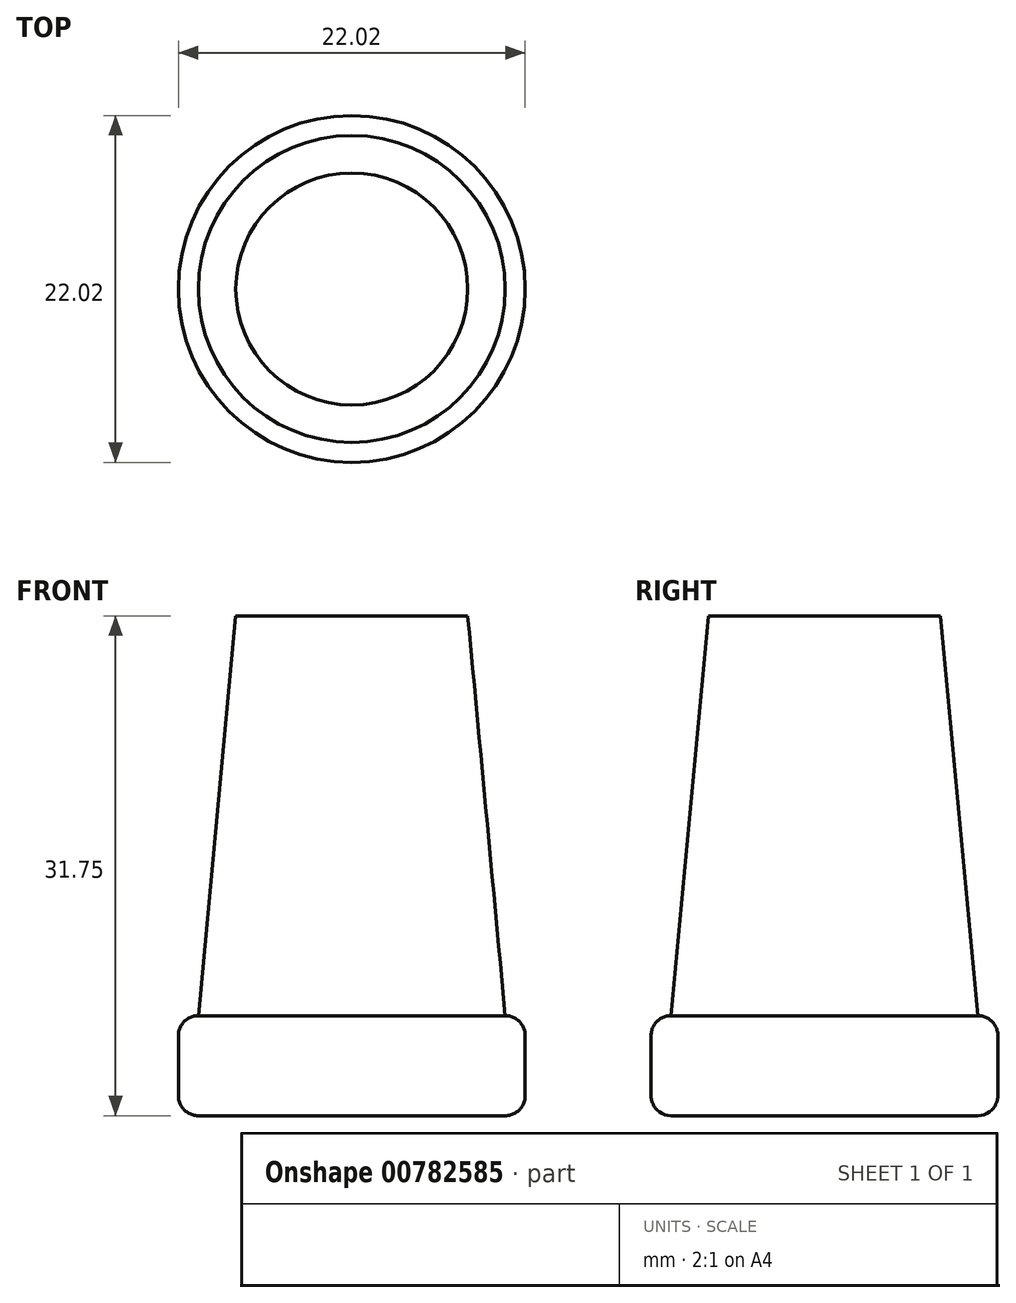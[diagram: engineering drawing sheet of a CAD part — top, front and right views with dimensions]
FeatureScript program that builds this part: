
annotation { "Feature Type Name" : "Feature", "Feature Type Description" : "" }
export const myFeature = defineFeature(function(context is Context, id is Id, definition is map)
    precondition{}
    {
        {
            var Q0;
            Q0=qCreatedBy(makeId("Top.planeOp"),FACE);
            var sketch = newSketch(context, id + "F0", { "sketchPlane" : qUnion([Q0])});
            skCircle(sketch, "E0", {"center": v(0, 0) * mm, "radius": 11.01 * mm});
            skSolve(sketch);
        }
        {
            var Q0;
            Q0 = qSketchRegion(id + "F0", true);
            extrude(context, id + "F1", {"entities" : qUnion([Q0]), "depth" : 6.35 * mm, "offsetDistance" : 25.4 * mm});
        }
        {
            var Q0;
            Q0=makeQuery(id+"F1.opExtrude","CAP_EDGE",EDGE,{"disambiguationData":[OSD([sQuery(id+"F0.wireOp",EDGE,"E0")])],"isStart":false});
            var Q1;
            Q1=makeQuery(id+"F1.opExtrude","CAP_EDGE",EDGE,{"disambiguationData":[OSD([sQuery(id+"F0.wireOp",EDGE,"E0")])],"isStart":true});
            fillet(context, id + "F2", {"entities" : qUnion([Q0, Q1]), "radius" : 1.27 * mm, "tangentPropagation" : true, "allowEdgeOverflow" : false});
        }
        {
            var Q0;
            Q0=qCreatedBy(makeId("Top.planeOp"),FACE);
            cPlane(context, id + "F3", {"entities" : qUnion([Q0]), "cplaneType" : CPlaneType.OFFSET, "offset" : 31.75 * mm, "width" : 152.4 * mm, "height" : 152.4 * mm});
        }
        {
            var Q0;
            Q0=qCreatedBy(id+"F3.planeOp",FACE);
            var sketch = newSketch(context, id + "F4", { "sketchPlane" : qUnion([Q0])});
            skCircle(sketch, "E1", {"center": v(0, 0) * mm, "radius": 7.37 * mm});
            skSolve(sketch);
        }
        {
            var Q1;
            Q1=makeQuery(id+"F1.opExtrude","CAP_FACE",FACE,{"disambiguationData":[OSD([sQuery(id+"F0.wireOp",EDGE,"E0")])],"isStart":false});
            var Q2;
            Q2=makeQuery(id+"F4.imprint","IMPRINT",FACE,{"disambiguationData":[TD([[makeQuery(id+"F4.imprint","IMPRINT",EDGE,{"derivedFrom":sQuery(id+"F4.wireOp",EDGE,"E1")}),1.0]])]});
            loft(context, id + "F5", {"operationType" : NewBodyOperationType.ADD, "sheetProfilesArray" : [{ "sheetProfileEntities" : qUnion([Q1]) }, { "sheetProfileEntities" : qUnion([Q2]) }]});
        }
    });
